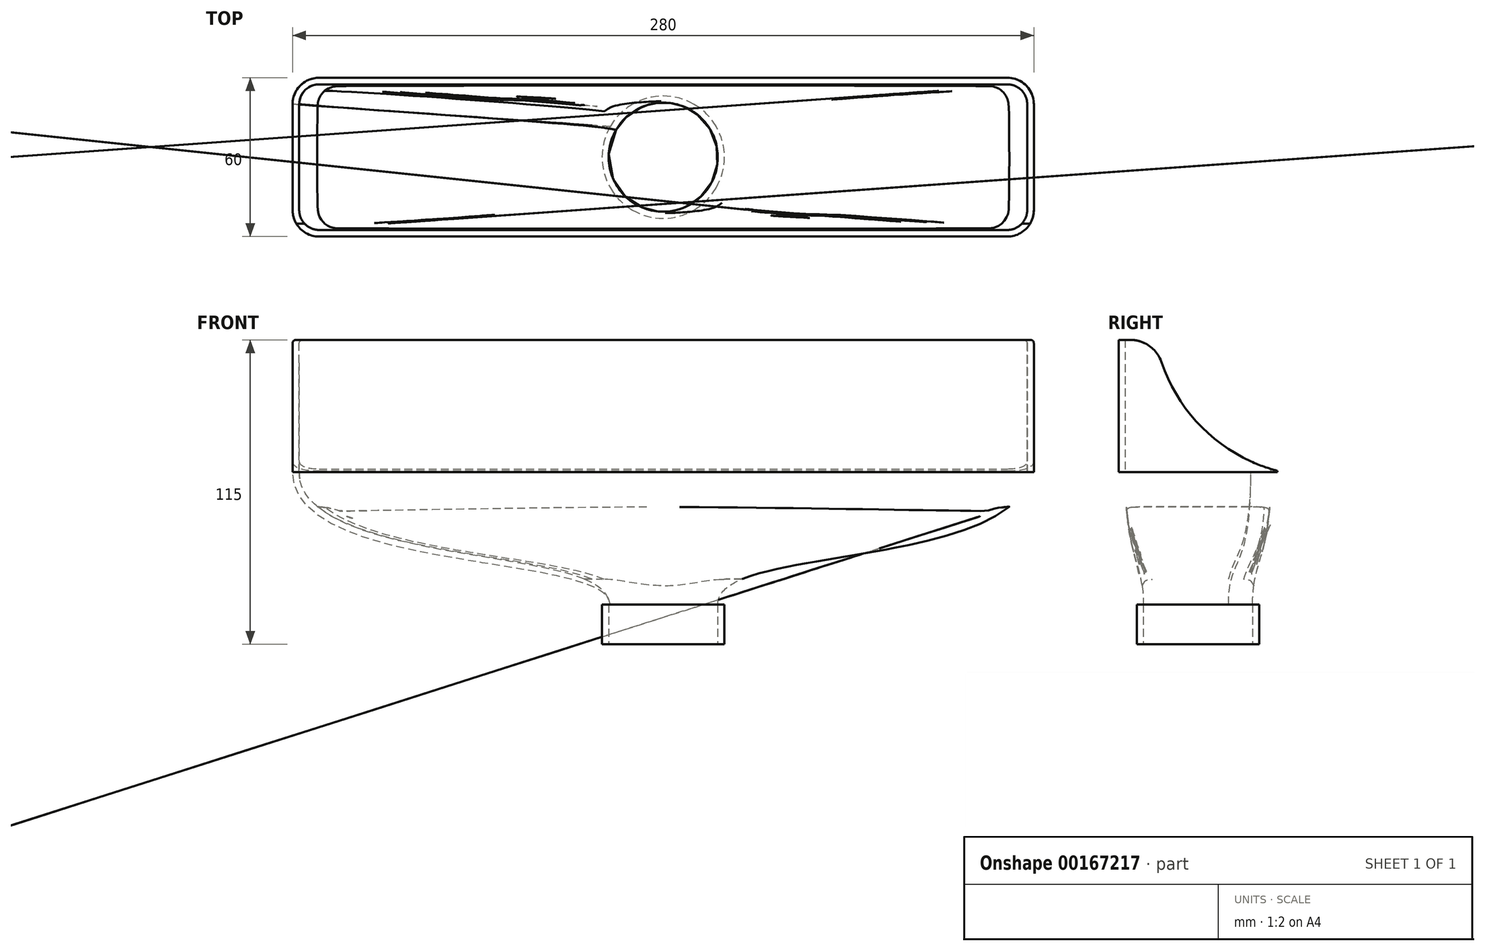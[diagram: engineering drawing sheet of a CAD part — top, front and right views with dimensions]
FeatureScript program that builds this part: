
annotation { "Feature Type Name" : "Feature", "Feature Type Description" : "" }
export const myFeature = defineFeature(function(context is Context, id is Id, definition is map)
    precondition{}
    {
        {
            var Q0;
            Q0=qCreatedBy(makeId("Top.planeOp"),FACE);
            var sketch = newSketch(context, id + "F0", { "sketchPlane" : qUnion([Q0])});
            skLineSegment(sketch, "E0", {"start": v(-20.01, 11.55) * mm, "end": v(20.01, -11.55) * mm, "construction": true});
            skLineSegment(sketch, "E1", {"start": v(20.01, 11.55) * mm, "end": v(-20.01, -11.55) * mm, "construction": true});
            skLineSegment(sketch, "E2", {"start": v(-11.55, 20.01) * mm, "end": v(11.55, -20.01) * mm, "construction": true});
            skLineSegment(sketch, "E3", {"start": v(-11.55, -20.01) * mm, "end": v(11.55, 20.01) * mm, "construction": true});
            skArc(sketch, "E4", {"start": v(-20.01, 11.55) * mm, "mid": v(-23.1, 0) * mm, "end": v(-20.01, -11.55) * mm});
            skArc(sketch, "E5", {"start": v(-11.55, 20.01) * mm, "mid": v(-16.34, 16.34) * mm, "end": v(-20.01, 11.55) * mm});
            skArc(sketch, "E6", {"start": v(11.55, 20.01) * mm, "mid": v(0, 23.1) * mm, "end": v(-11.55, 20.01) * mm});
            skArc(sketch, "E7", {"start": v(20.01, 11.55) * mm, "mid": v(16.34, 16.34) * mm, "end": v(11.55, 20.01) * mm});
            skArc(sketch, "E8", {"start": v(20.01, -11.55) * mm, "mid": v(23.1, 0) * mm, "end": v(20.01, 11.55) * mm});
            skArc(sketch, "E9", {"start": v(11.55, -20.01) * mm, "mid": v(16.34, -16.34) * mm, "end": v(20.01, -11.55) * mm});
            skArc(sketch, "E10", {"start": v(-11.55, -20.01) * mm, "mid": v(0, -23.1) * mm, "end": v(11.55, -20.01) * mm});
            skArc(sketch, "E11", {"start": v(-20.01, -11.55) * mm, "mid": v(-16.34, -16.34) * mm, "end": v(-11.55, -20.01) * mm});
            skSolve(sketch);
        }
        {
            var Q0;
            Q0=qCreatedBy(makeId("Top.planeOp"),FACE);
            cPlane(context, id + "F1", {"entities" : qUnion([Q0]), "cplaneType" : CPlaneType.OFFSET, "offset" : 50 * mm, "width" : 150 * mm, "height" : 150 * mm});
        }
        {
            var Q0;
            Q0=qCreatedBy(id+"F1.planeOp",FACE);
            var sketch = newSketch(context, id + "F2", { "sketchPlane" : qUnion([Q0])});
            skLineSegment(sketch, "E12.bottom", {"start": v(130, 30) * mm, "end": v(-130, 30) * mm});
            skLineSegment(sketch, "E12.top", {"start": v(130, -30) * mm, "end": v(-130, -30) * mm});
            skLineSegment(sketch, "E12.left", {"start": v(140, 20) * mm, "end": v(140, -20) * mm});
            skLineSegment(sketch, "E12.right", {"start": v(-140, 20) * mm, "end": v(-140, -20) * mm});
            skPoint(sketch, "E12.middle", {"position": v(0, 0) * mm});
            skPoint(sketch, "E13.visualSharp", {"position": v(-140, 30) * mm});
            skArc(sketch, "E13.filletArc", {"start": v(-130, 30) * mm, "mid": v(-137.07, 27.07) * mm, "end": v(-140, 20) * mm});
            skPoint(sketch, "E14.visualSharp", {"position": v(140, 30) * mm});
            skArc(sketch, "E14.filletArc", {"start": v(140, 20) * mm, "mid": v(137.07, 27.07) * mm, "end": v(130, 30) * mm});
            skPoint(sketch, "E15.visualSharp", {"position": v(140, -30) * mm});
            skArc(sketch, "E15.filletArc", {"start": v(130, -30) * mm, "mid": v(137.07, -27.07) * mm, "end": v(140, -20) * mm});
            skPoint(sketch, "E16.visualSharp", {"position": v(-140, -30) * mm});
            skArc(sketch, "E16.filletArc", {"start": v(-140, -20) * mm, "mid": v(-137.07, -27.07) * mm, "end": v(-130, -30) * mm});
            skSolve(sketch);
        }
        {
            var Q0;
            Q0=makeQuery(id+"F0.imprint","IMPRINT",FACE,{"disambiguationData":[TD([[makeQuery(id+"F0.imprint","IMPRINT",EDGE,{"derivedFrom":sQuery(id+"F0.wireOp",EDGE,"E4")}),1.0]])]});
            var Q1;
            Q1=makeQuery(id+"F2.imprint","IMPRINT",FACE,{"disambiguationData":[TD([[makeQuery(id+"F2.imprint","IMPRINT",EDGE,{"derivedFrom":sQuery(id+"F2.wireOp",EDGE,"E12.bottom")}),1.0]])]});
            loft(context, id + "F3", {"startCondition" : LoftEndDerivativeType.NORMAL_TO_PROFILE, "startMagnitude" : 1, "endCondition" : LoftEndDerivativeType.NORMAL_TO_PROFILE, "endMagnitude" : 2, "sheetProfilesArray" : [{ "sheetProfileEntities" : qUnion([Q0]) }, { "sheetProfileEntities" : qUnion([Q1]) }]});
        }
        {
            var Q0;
            Q0=makeQuery(id+"F3.opLoft","CAP_FACE",FACE,{"disambiguationData":[OSD([makeQuery(id+"F2.imprint","IMPRINT",FACE,{"disambiguationData":[TD([[makeQuery(id+"F2.imprint","IMPRINT",EDGE,{"derivedFrom":sQuery(id+"F2.wireOp",EDGE,"E12.bottom")}),1.0]])]})])],"isStart":true});
            extrude(context, id + "F4", {"entities" : qUnion([Q0]), "operationType" : NewBodyOperationType.ADD, "depth" : 50 * mm});
        }
        {
            var Q0;
            Q0=makeQuery(id+"F3.opLoft","CAP_FACE",FACE,{"disambiguationData":[OSD([makeQuery(id+"F0.imprint","IMPRINT",FACE,{"disambiguationData":[TD([[makeQuery(id+"F0.imprint","IMPRINT",EDGE,{"derivedFrom":sQuery(id+"F0.wireOp",EDGE,"E4")}),1.0]])]})])],"isStart":true});
            extrude(context, id + "F5", {"entities" : qUnion([Q0]), "operationType" : NewBodyOperationType.ADD, "depth" : 15 * mm});
        }
        {
            var Q0;
            Q0=makeQuery(id+"F4.opExtrude","CAP_FACE",FACE,{"disambiguationData":[OSD([makeQuery(id+"F2.imprint","IMPRINT",FACE,{"disambiguationData":[TD([[makeQuery(id+"F2.imprint","IMPRINT",EDGE,{"derivedFrom":sQuery(id+"F2.wireOp",EDGE,"E12.bottom")}),1.0]])]})])],"isStart":false});
            var Q1;
            Q1=makeQuery(id+"F5.opExtrude","CAP_FACE",FACE,{"disambiguationData":[OSD([makeQuery(id+"F0.imprint","IMPRINT",FACE,{"disambiguationData":[TD([[makeQuery(id+"F0.imprint","IMPRINT",EDGE,{"derivedFrom":sQuery(id+"F0.wireOp",EDGE,"E4")}),1.0]])]})])],"isStart":false});
            shell(context, id + "F6", {"entities" : qUnion([Q0, Q1]), "thickness" : 2.5 * mm});
        }
        {
            var Q0;
            Q0=qCreatedBy(makeId("Right.planeOp"),FACE);
            var sketch = newSketch(context, id + "F7", { "sketchPlane" : qUnion([Q0])});
            skLineSegment(sketch, "E17", {"start": v(-25.77, 100.02) * mm, "end": v(30.14, 100.02) * mm});
            skLineSegment(sketch, "E18", {"start": v(30.14, 100.02) * mm, "end": v(30.14, 50.48) * mm});
            skArc(sketch, "E19", {"start": v(-13.66, 91.34) * mm, "mid": v(3.1, 65.4) * mm, "end": v(30.14, 50.48) * mm});
            skArc(sketch, "E20", {"start": v(-13.66, 91.34) * mm, "mid": v(-18.32, 97.63) * mm, "end": v(-25.77, 100.02) * mm});
            skSolve(sketch);
        }
        {
            var Q0;
            Q0=makeQuery(id+"F7.imprint","IMPRINT",FACE,{"disambiguationData":[TD([[makeQuery(id+"F7.imprint","IMPRINT",EDGE,{"derivedFrom":sQuery(id+"F7.wireOp",EDGE,"E17")}),-1.0]])]});
            extrude(context, id + "F8", {"entities" : qUnion([Q0]), "operationType" : NewBodyOperationType.REMOVE, "endBound" : BoundingType.THROUGH_ALL, "oppositeDirection" : true, "depth" : 25 * mm, "hasSecondDirection" : true, "secondDirectionBound" : SecondDirectionBoundingType.THROUGH_ALL, "secondDirectionOppositeDirection" : false, "secondDirectionDepth" : 25 * mm});
        }
    });
